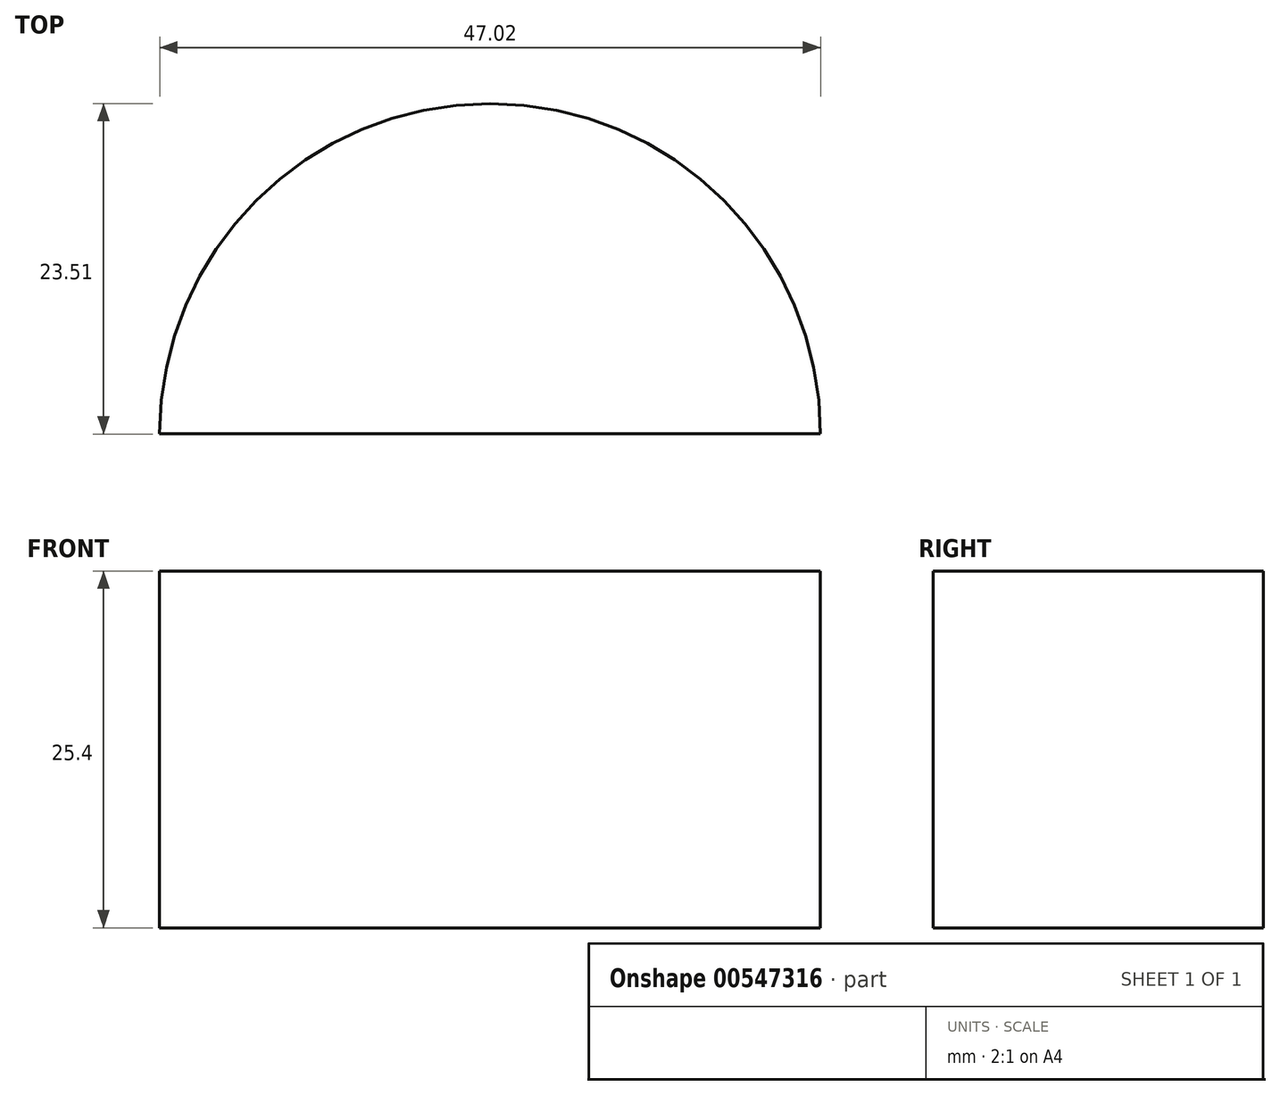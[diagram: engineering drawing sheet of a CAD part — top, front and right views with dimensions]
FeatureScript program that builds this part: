
annotation { "Feature Type Name" : "Feature", "Feature Type Description" : "" }
export const myFeature = defineFeature(function(context is Context, id is Id, definition is map)
    precondition{}
    {
        {
            var Q0;
            Q0=qCreatedBy(makeId("Top.planeOp"),FACE);
            var sketch = newSketch(context, id + "F0", { "sketchPlane" : qUnion([Q0])});
            skCircle(sketch, "E0", {"center": v(-37.41, 49.74) * mm, "radius": 23.5 * mm});
            skSolve(sketch);
        }
        {
            var Q0;
            Q0=makeQuery(id+"F0.imprint","IMPRINT",FACE,{"disambiguationData":[TD([[makeQuery(id+"F0.imprint","IMPRINT",EDGE,{"derivedFrom":sQuery(id+"F0.wireOp",EDGE,"E0")}),1.0]])]});
            extrude(context, id + "F1", {"entities" : qUnion([Q0]), "depth" : 25.4 * mm, "offsetDistance" : 25.4 * mm});
        }
        {
            var Q0;
            Q0=makeQuery(id+"F1.opExtrude","CAP_FACE",FACE,{"disambiguationData":[OSD([sQuery(id+"F0.wireOp",EDGE,"E0")])],"isStart":false});
            var sketch = newSketch(context, id + "F2", { "sketchPlane" : qUnion([Q0])});
            skLineSegment(sketch, "E1", {"start": v(-37.41, 49.74) * mm, "end": v(-13.9, 49.74) * mm});
            skLineSegment(sketch, "E2", {"start": v(-37.41, 49.74) * mm, "end": v(-60.92, 49.74) * mm});
            skSolve(sketch);
        }
        {
            var Q0;
            Q0 = qSketchRegion(id + "F2", true);
            var Q1;
            {var subQ0=sQuery(id+"F2.wireOp",EDGE,"E1");Q1=makeQuery(id+"F2.imprint","IMPRINT",FACE,{"disambiguationData":[TD([[makeQuery(id+"F2.imprint","IMPRINT",EDGE,{"derivedFrom":subQ0}),-1.0]])]});}
            extrude(context, id + "F3", {"entities" : qUnion([Q0, Q1]), "operationType" : NewBodyOperationType.REMOVE, "oppositeDirection" : true, "depth" : 25.4 * mm, "offsetDistance" : 25.4 * mm});
        }
    });
